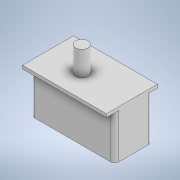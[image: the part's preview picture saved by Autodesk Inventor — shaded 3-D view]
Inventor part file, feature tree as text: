
AUTODESK INVENTOR PART (.ipt)
format: ipt  version: 2021 (Build 250183000, 183)  size: 174,080 bytes
history: native  units: in
note: dims shown in document units (in); Inventor stores cm internally (conversion verified against a paired STEP export)
features: extrude x4, sketch x4
ambient origin geometry x8: Origin, YZ Plane, XZ Plane, XY Plane, X Axis, Y Axis, Z Axis, Center Point
bodies: Solid1 (feature_tree)
feature tree (8):
  extrude  "Extrusion1"  Depth=0.9in
  extrude  "Extrusion8"  Depth=0.1in
  extrude  "Extrusion9"  Depth=0.09in
  extrude  "Extrusion10"  Depth=0.0787in
  sketch  "Sketch1"  dims[d0=2.0in d1=0.9in]
  sketch  "Sketch8"  dims[d2=0.1in d3=0.1in]
  sketch  "Sketch9"  dims[d4=0.09in d5=0.09in]
  sketch  "Sketch10"  dims[d6=0.7in d7=0.75in d9=0.35in d10=0.1in d11=0.1in d12=0.375in d13=0.1in d14=0.1in d15=0.1in d16=1.1417in d17=0.0in d62=0.2953in d63=0.1in d64=0.8661in d65=0.5906in d66=0.0in d67=0.315in d68=0.1575in d69=0.0984in d70=0.0984in d71=0.0787in d72=0.0in d73=0.1969in d74=0.1181in d75=0.0787in d76=0.0in]
